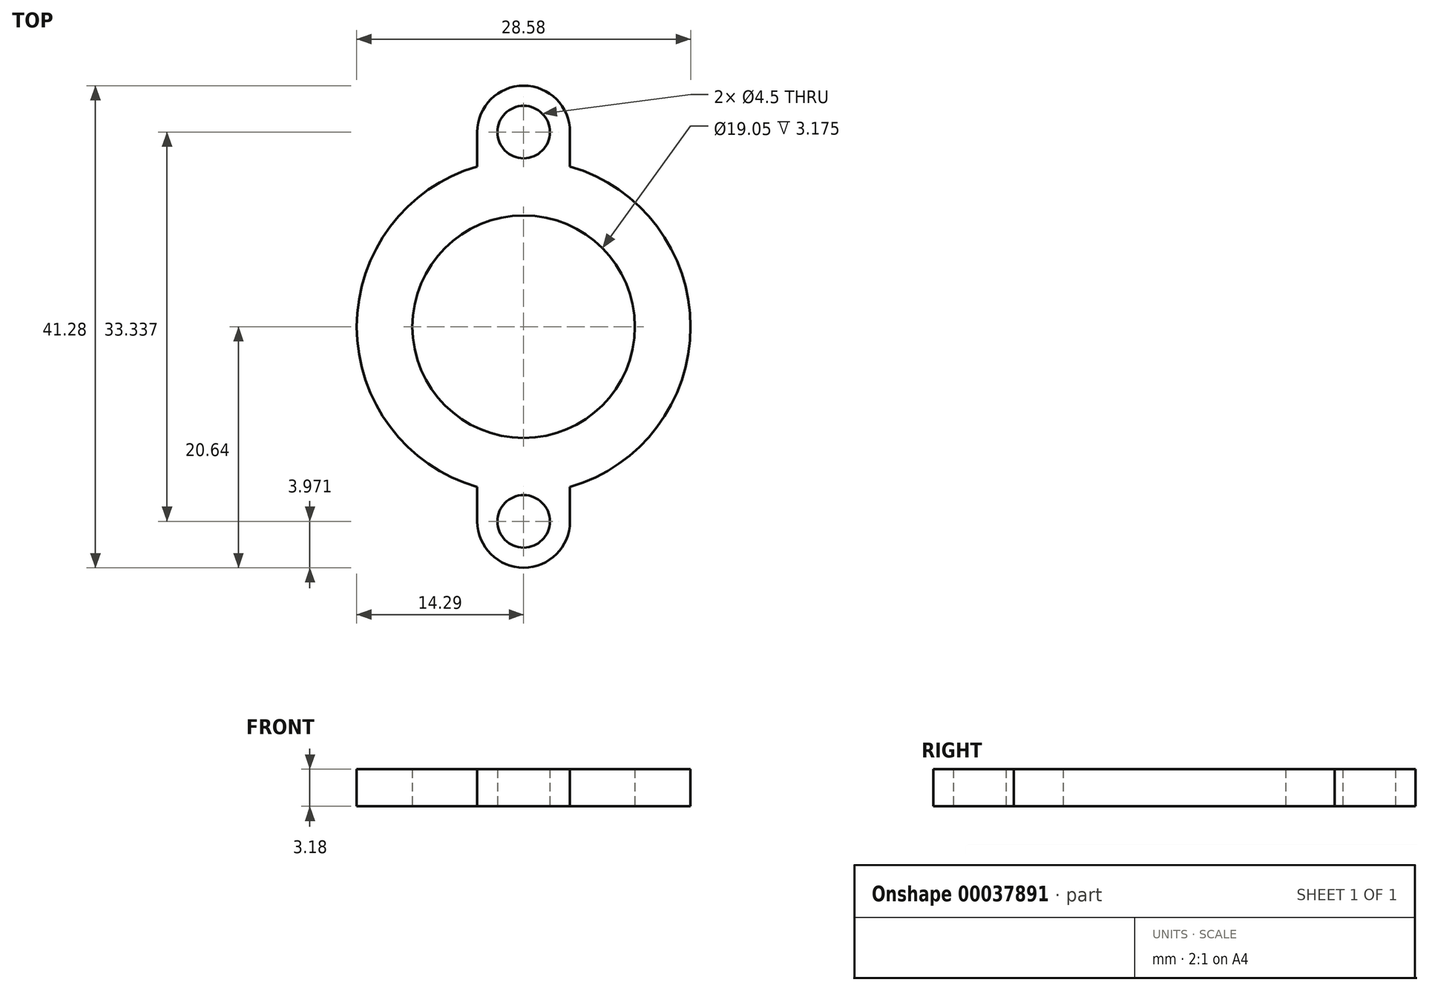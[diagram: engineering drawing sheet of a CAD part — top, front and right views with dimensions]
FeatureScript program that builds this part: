
annotation { "Feature Type Name" : "Feature", "Feature Type Description" : "" }
export const myFeature = defineFeature(function(context is Context, id is Id, definition is map)
    precondition{}
    {
        {
            var Q0;
            Q0=qCreatedBy(makeId("Top.planeOp"),FACE);
            var sketch = newSketch(context, id + "F0", { "sketchPlane" : qUnion([Q0])});
            skCircle(sketch, "E0", {"center": v(0, 0) * mm, "radius": 9.53 * mm});
            skArc(sketch, "E1", {"start": v(3.97, -13.73) * mm, "mid": v(14.29, 0) * mm, "end": v(3.97, 13.73) * mm});
            skArc(sketch, "E2", {"start": v(-3.97, 13.73) * mm, "mid": v(-14.29, 0) * mm, "end": v(-3.97, -13.73) * mm});
            skLineSegment(sketch, "E3", {"start": v(0, -16.67) * mm, "end": v(0, 16.67) * mm, "construction": true});
            skLineSegment(sketch, "E4", {"start": v(-3.97, 16.67) * mm, "end": v(3.97, 16.67) * mm, "construction": true});
            skLineSegment(sketch, "E5", {"start": v(-3.97, 16.67) * mm, "end": v(-3.97, 13.73) * mm});
            skLineSegment(sketch, "E6", {"start": v(3.97, 16.67) * mm, "end": v(3.97, 13.73) * mm});
            skLineSegment(sketch, "E7", {"start": v(-3.97, -16.67) * mm, "end": v(3.97, -16.67) * mm, "construction": true});
            skLineSegment(sketch, "E8", {"start": v(3.97, -16.67) * mm, "end": v(3.97, -13.73) * mm});
            skLineSegment(sketch, "E9", {"start": v(-3.97, -16.67) * mm, "end": v(-3.97, -13.73) * mm});
            skArc(sketch, "E10", {"start": v(3.97, 16.67) * mm, "mid": v(0, 20.64) * mm, "end": v(-3.97, 16.67) * mm});
            skArc(sketch, "E11", {"start": v(-3.97, -16.67) * mm, "mid": v(0, -20.64) * mm, "end": v(3.97, -16.67) * mm});
            skCircle(sketch, "E12", {"center": v(0, 16.67) * mm, "radius": 2.25 * mm});
            skCircle(sketch, "E13", {"center": v(0, -16.67) * mm, "radius": 2.25 * mm});
            skSolve(sketch);
        }
        {
            var Q0;
            Q0=qSketchRegion(id+"F0",true);
            extrude(context, id + "F1", {"entities" : qUnion([Q0]), "depth" : 3.17 * mm});
        }
    });
